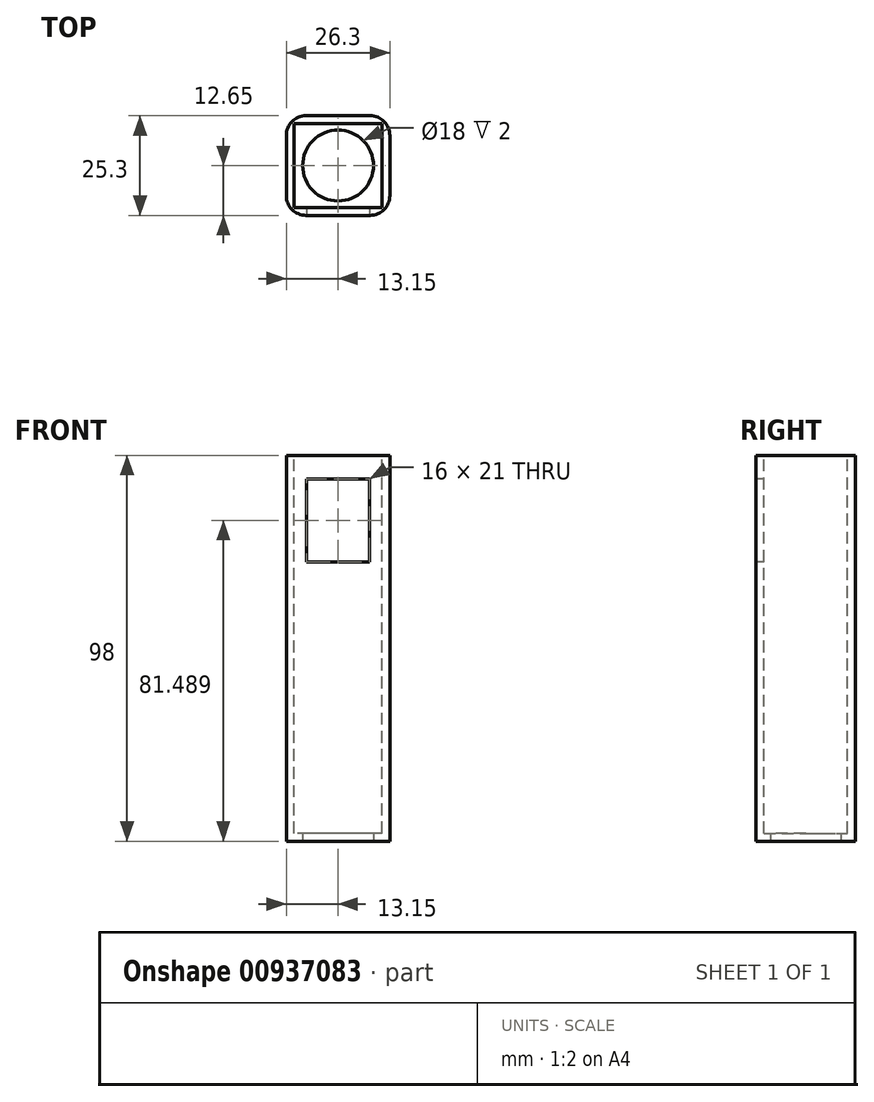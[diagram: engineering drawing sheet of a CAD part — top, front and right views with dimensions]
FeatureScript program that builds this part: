
annotation { "Feature Type Name" : "Feature", "Feature Type Description" : "" }
export const myFeature = defineFeature(function(context is Context, id is Id, definition is map)
    precondition{}
    {
        {
            var Q0;
            Q0=qCreatedBy(makeId("Top.planeOp"),FACE);
            var sketch = newSketch(context, id + "F0", { "sketchPlane" : qUnion([Q0])});
            skLineSegment(sketch, "E0.bottom", {"start": v(13.15, -12.65) * mm, "end": v(-13.15, -12.65) * mm});
            skLineSegment(sketch, "E0.top", {"start": v(13.15, 12.65) * mm, "end": v(-13.15, 12.65) * mm});
            skLineSegment(sketch, "E0.left", {"start": v(13.15, -12.65) * mm, "end": v(13.15, 12.65) * mm});
            skLineSegment(sketch, "E0.right", {"start": v(-13.15, -12.65) * mm, "end": v(-13.15, 12.65) * mm});
            skPoint(sketch, "E0.middle", {"position": v(0, 0) * mm});
            skSolve(sketch);
        }
        {
            var Q0;
            Q0=makeQuery(id+"F0.imprint","IMPRINT",FACE,{"disambiguationData":[TD([[makeQuery(id+"F0.imprint","IMPRINT",EDGE,{"derivedFrom":sQuery(id+"F0.wireOp",EDGE,"E0.bottom")}),-1.0]])]});
            extrude(context, id + "F1", {"entities" : qUnion([Q0]), "oppositeDirection" : true, "depth" : 98 * mm, "offsetDistance" : 25 * mm});
        }
        {
            var Q0;
            Q0=makeQuery(id+"F1.opExtrude","CAP_FACE",FACE,{"disambiguationData":[OSD([sQuery(id+"F0.wireOp",EDGE,"E0.bottom"),sQuery(id+"F0.wireOp",EDGE,"E0.top"),sQuery(id+"F0.wireOp",EDGE,"E0.left"),sQuery(id+"F0.wireOp",EDGE,"E0.right")])],"isStart":true});
            shell(context, id + "F2", {"entities" : qUnion([Q0]), "thickness" : 2 * mm});
        }
        {
            var Q0;
            Q0=makeQuery(id+"F1.opExtrude","CAP_FACE",FACE,{"disambiguationData":[OSD([sQuery(id+"F0.wireOp",EDGE,"E0.bottom"),sQuery(id+"F0.wireOp",EDGE,"E0.top"),sQuery(id+"F0.wireOp",EDGE,"E0.left"),sQuery(id+"F0.wireOp",EDGE,"E0.right")])],"isStart":false});
            var sketch = newSketch(context, id + "F3", { "sketchPlane" : qUnion([Q0])});
            skCircle(sketch, "E1", {"center": v(0, 0) * mm, "radius": 9 * mm});
            skSolve(sketch);
        }
        {
            var Q0;
            Q0=makeQuery(id+"F3.imprint","IMPRINT",FACE,{"disambiguationData":[TD([[makeQuery(id+"F3.imprint","IMPRINT",EDGE,{"derivedFrom":sQuery(id+"F3.wireOp",EDGE,"E1")}),1.0]])]});
            extrude(context, id + "F4", {"entities" : qUnion([Q0]), "operationType" : NewBodyOperationType.REMOVE, "oppositeDirection" : true, "depth" : 25 * mm, "offsetDistance" : 25 * mm});
        }
        {
            var Q0;
            Q0=makeQuery(id+"F1.opExtrude","SWEPT_FACE",FACE,{"disambiguationData":[OSD([sQuery(id+"F0.wireOp",EDGE,"E0.bottom")])]});
            var sketch = newSketch(context, id + "F5", { "sketchPlane" : qUnion([Q0])});
            skLineSegment(sketch, "E2", {"start": v(0, 0) * mm, "end": v(0, -6) * mm});
            skSolve(sketch);
        }
        {
            var Q0;
            {var subQ0=sQuery(id+"F0.wireOp",EDGE,"E0.bottom");Q0=makeQuery(id+"F5.imprint","IMPRINT",FACE,{"disambiguationData":[TD([[makeQuery(id+"F5.imprint","IMPRINT",EDGE,{"derivedFrom":makeQuery(id+"F1.opExtrude","CAP_EDGE",EDGE,{"disambiguationData":[OSD([subQ0])],"isStart":false})}),-1.0]])]});}
            var sketch = newSketch(context, id + "F6", { "sketchPlane" : qUnion([Q0])});
            skLineSegment(sketch, "E3.bottom", {"start": v(8, -27.01) * mm, "end": v(-8, -27.01) * mm});
            skLineSegment(sketch, "E3.top", {"start": v(8, -6.01) * mm, "end": v(-8, -6.01) * mm});
            skLineSegment(sketch, "E3.left", {"start": v(8, -27.01) * mm, "end": v(8, -6.01) * mm});
            skLineSegment(sketch, "E3.right", {"start": v(-8, -27.01) * mm, "end": v(-8, -6.01) * mm});
            skPoint(sketch, "E3.middle", {"position": v(0, -16.51) * mm});
            skSolve(sketch);
        }
        {
            var Q0;
            Q0=makeQuery(id+"F6.imprint","IMPRINT",FACE,{"disambiguationData":[TD([[makeQuery(id+"F6.imprint","IMPRINT",EDGE,{"derivedFrom":sQuery(id+"F6.wireOp",EDGE,"E3.bottom")}),-1.0]])]});
            extrude(context, id + "F7", {"entities" : qUnion([Q0]), "operationType" : NewBodyOperationType.REMOVE, "oppositeDirection" : true, "depth" : 2 * mm, "offsetDistance" : 25 * mm});
        }
        {
            var Q0;
            Q0=makeQuery(id+"F1.opExtrude","SWEPT_EDGE",EDGE,{"disambiguationData":[OSD([sQuery(id+"F0.wireOp",EDGE,"E0.bottom"),sQuery(id+"F0.wireOp",EDGE,"E0.right")])]});
            var Q1;
            Q1=makeQuery(id+"F1.opExtrude","SWEPT_EDGE",EDGE,{"disambiguationData":[OSD([sQuery(id+"F0.wireOp",EDGE,"E0.bottom"),sQuery(id+"F0.wireOp",EDGE,"E0.left")])]});
            var Q2;
            Q2=makeQuery(id+"F1.opExtrude","SWEPT_EDGE",EDGE,{"disambiguationData":[OSD([sQuery(id+"F0.wireOp",EDGE,"E0.top"),sQuery(id+"F0.wireOp",EDGE,"E0.left")])]});
            var Q3;
            Q3=makeQuery(id+"F1.opExtrude","SWEPT_EDGE",EDGE,{"disambiguationData":[OSD([sQuery(id+"F0.wireOp",EDGE,"E0.top"),sQuery(id+"F0.wireOp",EDGE,"E0.right")])]});
            fillet(context, id + "F8", {"entities" : qUnion([Q0, Q1, Q2, Q3]), "radius" : 5 * mm, "tangentPropagation" : true, "allowEdgeOverflow" : false});
        }
    });
